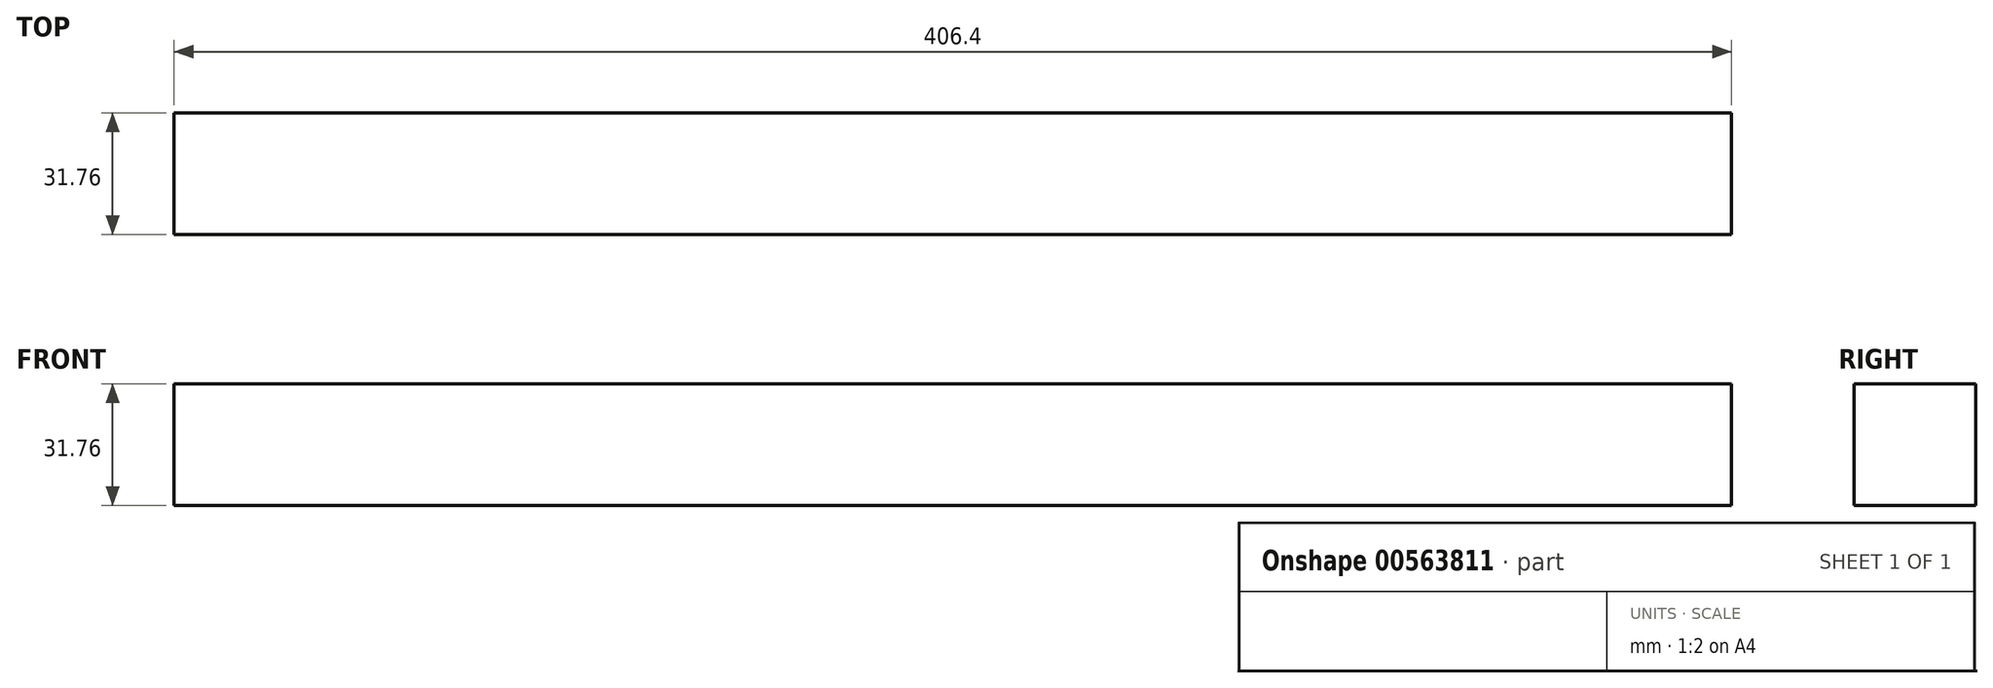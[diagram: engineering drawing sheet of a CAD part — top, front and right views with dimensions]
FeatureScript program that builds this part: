
annotation { "Feature Type Name" : "Feature", "Feature Type Description" : "" }
export const myFeature = defineFeature(function(context is Context, id is Id, definition is map)
    precondition{}
    {
        {
            var Q0;
            Q0=qCreatedBy(makeId("Front.planeOp"),FACE);
            var sketch = newSketch(context, id + "F0", { "sketchPlane" : qUnion([Q0])});
            skLineSegment(sketch, "E0.bottom", {"start": v(-203.2, 15.87) * mm, "end": v(203.2, 15.87) * mm});
            skLineSegment(sketch, "E0.top", {"start": v(-203.2, -15.88) * mm, "end": v(203.2, -15.88) * mm});
            skLineSegment(sketch, "E0.left", {"start": v(-203.2, 15.87) * mm, "end": v(-203.2, -15.88) * mm});
            skLineSegment(sketch, "E0.right", {"start": v(203.2, 15.87) * mm, "end": v(203.2, -15.88) * mm});
            skPoint(sketch, "E0.middle", {"position": v(0, 0) * mm});
            skSolve(sketch);
        }
        {
            var Q0;
            Q0=makeQuery(id+"F0.imprint","IMPRINT",FACE,{"disambiguationData":[TD([[makeQuery(id+"F0.imprint","IMPRINT",EDGE,{"derivedFrom":sQuery(id+"F0.wireOp",EDGE,"E0.bottom")}),-1.0]])]});
            extrude(context, id + "F1", {"entities" : qUnion([Q0]), "endBound" : BoundingType.SYMMETRIC, "depth" : 31.75 * mm, "offsetDistance" : 25.4 * mm});
        }
    });
